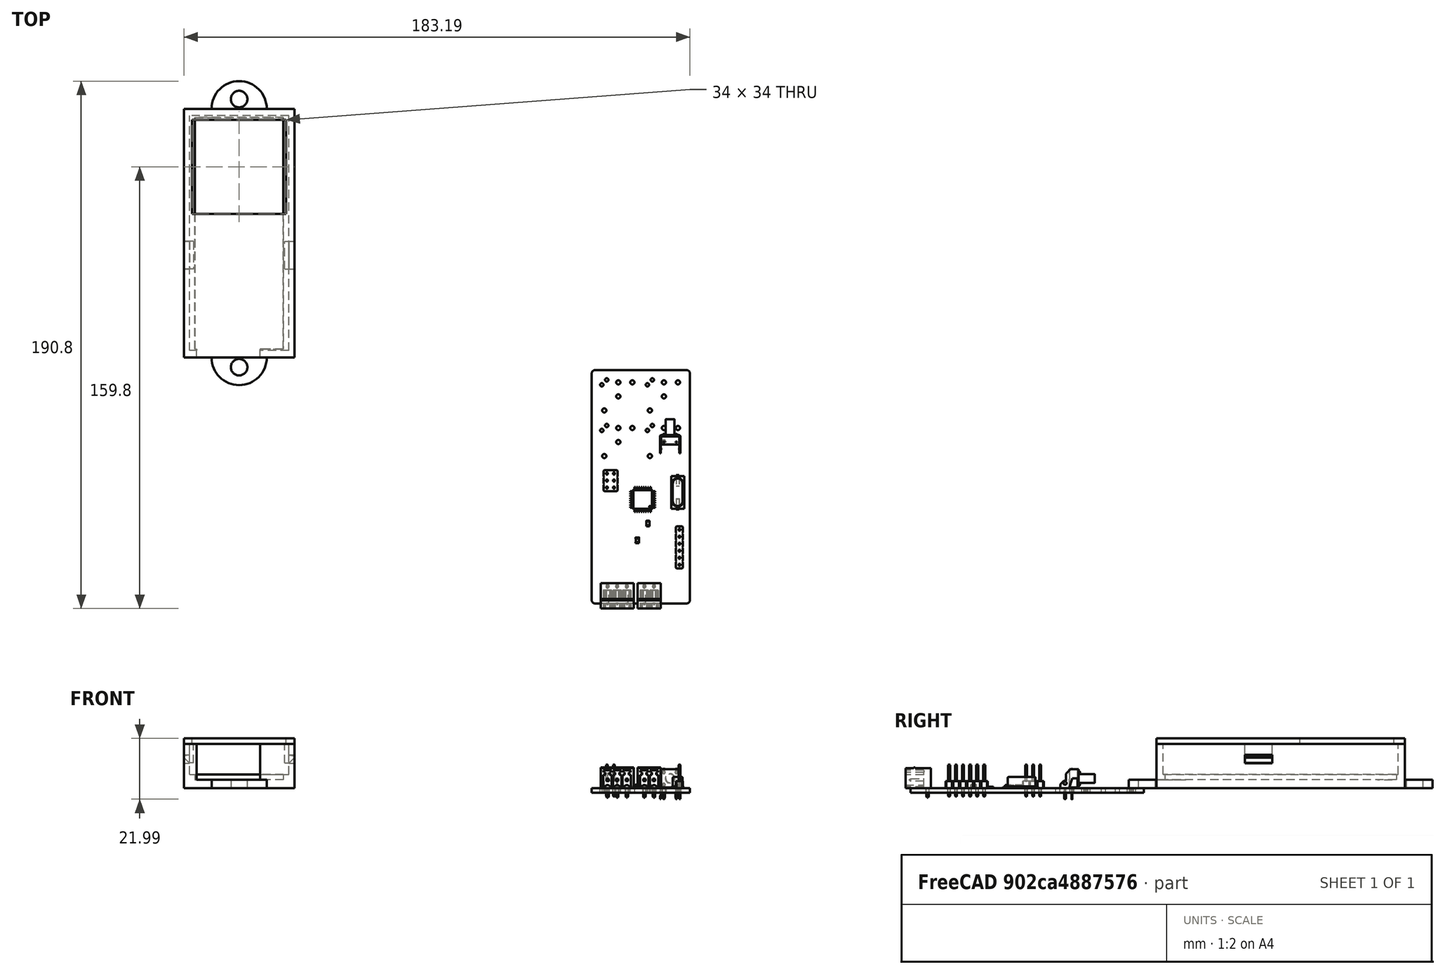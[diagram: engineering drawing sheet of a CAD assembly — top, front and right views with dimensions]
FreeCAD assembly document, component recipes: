
FREECAD ASSEMBLY — COMPONENT RECIPES ("doboz_v3")

This assembly document has 2 components, labeled P0..P1 below (a component is one placed body or linked part). 1 of them carries a construction recipe — the FreeCAD feature program that regenerates the part from scratch, quoted from this document or its linked companion documents; the rest are supplied as boundary geometry only. No exploded tour is included for this assembly.
COMPONENT P0 — geometry summary ("SEM_ProjektoroSCH-Rev2"; no construction recipe available for this part):
  bounding box: 86.3 x 35.6 x 12.5 mm
  tessellated surface: 117,506 triangles
  volume: 6876 mm^3 (18% of its bounding box)
COMPONENT P1 — recipe-attached ("Body", modeled in this document).
Construction recipe (the document's own serialized feature program — sketch geometry with constraints, then the solid features built on it; lengths are millimeters unless a unit is written):

FEATURE [Sketcher::SketchObject] Sketch
  FullyConstrained = true
  MapMode = 5
  Support = -> [XY_Plane004]
  sketch-geometry (4):
    g0: LineSegment StartX=-20 StartY=45 StartZ=0 EndX=20 EndY=45 EndZ=0
    g1: LineSegment StartX=20 StartY=45 StartZ=0 EndX=20 EndY=-45 EndZ=0
    g2: LineSegment StartX=20 StartY=-45 StartZ=0 EndX=-20 EndY=-45 EndZ=0
    g3: LineSegment StartX=-20 StartY=-45 StartZ=0 EndX=-20 EndY=45 EndZ=0
  constraints (11):
    c: Coincident(g0,g1)
    c: Coincident(g1,g2)
    c: Coincident(g2,g3)
    c: Coincident(g3,g0)
    c: Horizontal(g0)
    c: Horizontal(g2)
    c: Vertical(g1)
    c: Vertical(g3)
    c: Symmetric(g2,g0,g-1)
    c: DistanceX(g0,g0) = 40
    c: DistanceY(g1,g1) = 90
FEATURE [PartDesign::Pad] Pad
  Direction = (0,0,1)
  Length = 16
  Length2 = 10
  Profile = -> Sketch
  ReferenceAxis = -> Sketch [N_Axis]
  Type = 0
FEATURE [Sketcher::SketchObject] Sketch001
  FullyConstrained = true
  MapMode = 5
  Placement = pos=(0,0,16) rot=(0,0,1;0rad)
  Support = -> [Pad]
  sketch-geometry (4):
    g0: LineSegment StartX=-16 StartY=41.875 StartZ=0 EndX=16 EndY=41.875 EndZ=0
    g1: LineSegment StartX=16 StartY=41.875 StartZ=0 EndX=16 EndY=-41.875 EndZ=0
    g2: LineSegment StartX=16 StartY=-41.875 StartZ=0 EndX=-16 EndY=-41.875 EndZ=0
    g3: LineSegment StartX=-16 StartY=-41.875 StartZ=0 EndX=-16 EndY=41.875 EndZ=0
  constraints (11):
    c: Coincident(g0,g1)
    c: Coincident(g1,g2)
    c: Coincident(g2,g3)
    c: Coincident(g3,g0)
    c: Horizontal(g0)
    c: Horizontal(g2)
    c: Vertical(g1)
    c: Vertical(g3)
    c: Symmetric(g2,g0,g-1)
    c: DistanceX(g0,g0) = 32
    c: DistanceY(g1,g1) = 83.75
FEATURE [PartDesign::Pocket] Pocket
  BaseFeature = -> Pad
  Direction = (0,0,-1)
  Length = 13
  Length2 = 5
  Profile = -> Sketch001
  ReferenceAxis = -> Sketch001 [N_Axis]
  Type = 0
FEATURE [PartDesign::Body] Body
  Group = -> [Sketch,Pad,Sketch001,Pocket]
  Origin = -> Origin004
  Tip = -> Pocket
PROVENANCE & LICENSES
A FreeCAD (.FCStd) document from a public repository crawl; recipes are the document's own serialized feature recipes (and, for linked parts, companion documents' recipes).
License: mit.
